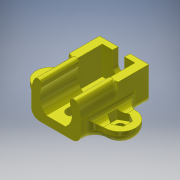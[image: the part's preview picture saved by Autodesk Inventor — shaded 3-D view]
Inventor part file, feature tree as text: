
AUTODESK INVENTOR PART (.ipt)
format: ipt  version: 2019.4 (Build 234330000, 330)  size: 492,544 bytes
history: native  units: mm
features: extrude x18, other x12, sketch x9, fillet x8, projected_geometry x3, chamfer x1, mirror x1
ambient origin geometry x8: Origin, YZ Plane, XZ Plane, XY Plane, X Axis, Y Axis, Z Axis, Center Point
bodies: Solid1 (feature_tree)
feature tree (52):
  extrude  "Body Clip Bulk"  Depth=7.0mm
  fillet  "Clip Bottom Fillet"  Radius=5.0mm
  other  "BC Midplane"
  extrude  "BC Top Cut"  Depth=3.0mm
  fillet  "BC Top Edge Fillets"  Radius=3.0mm
  extrude  "BC Removal Slot"  Depth=13.8mm
  extrude  "FS Floor Bulk"  Depth=2.0mm
  fillet  "FS Bottom Fillet"  Radius=10.4mm
  extrude  "FS Walls"  Depth=15.0mm
  extrude  "FS Front Shaft Seat"  Depth=1.4mm
  extrude  "FS Pillars"  Depth=2.6mm
  extrude  "BC 45deg cut"  TaperAngle=0.0deg  [1 undecoded]
  other  "Encoder Section Plane"
  extrude  "ES Floor"  Depth=10.0mm
  fillet  "ES Bottom Fillet"  Radius=2.0mm
  extrude  "ES Walls"  Depth=3.0mm
  extrude  "ES Slot"  Depth=10.0mm
  extrude  "ES Rear Cutaway"  Depth=10.0mm
  fillet  "ES Merge Fillet"  Radius=10.4mm
  fillet  "ES Cutaway Fille"  [1 undecoded]
  extrude  "ES Pins Undercut"  Depth=9.0mm
  chamfer  "ES Pins Undercut CHamfer"  Distance=7.8mm
  other  "Midplane"
  extrude  "Wing Bulk"  Depth=4.4mm
  extrude  "Wing Underside Merge"  Depth=10.0mm
  fillet  "Wing UNderside Fillet"  Radius=4.4mm
  extrude  "Wing Nut Cut"  Depth=2.0mm
  mirror  "Wing Mirror"
  fillet  "Wings Top Fillet"  [1 undecoded]
  extrude  "Slot Enlarging"  Depth=10.0mm
  extrude  "Extrusion18"  Depth=10.0mm
  other  "Body  Clip Bulk OL"
  other  "BC Top Cut OL"
  other  "FS Floor Bulk OL"
  other  "FS Walls OL"
  other  "FS Shaft Slot Seat OL"
  other  "FS Pillars OL"
  sketch  "Sketch9"  dims[d1=7.0mm d3=12.0mm d4=5.0mm]
  sketch  "Sketch10"  dims[d5=10.0mm d6=3.0mm d8=3.0mm]
  other  "ES walls OL"
  other  "ES Slot ol"
  sketch  "Sketch13"  dims[d9=18.0mm d10=13.8mm]
  other  "BC Removal Slot OL"
  sketch  "Sketch16"  dims[d11=0.0mm d12=2.0mm d13=10.4mm]
  projected_geometry  "Projected Loop1"
  sketch  "Sketch17"  dims[d14=13.8mm d15=15.0mm]
  sketch  "Sketch18"  dims[d16=0.0mm d18=1.4mm]
  projected_geometry  "Projected Loop2"
  sketch  "Sketch19"  dims[d19=18.0mm d20=2.6mm]
  sketch  "Sketch20"  dims[d21=11.2mm d22=0.0mm]
  projected_geometry  "Projected Loop3"
  sketch  "Sketch21"  dims[d23=3.0mm d24=6.8mm d25=2.0mm d26=3.0mm d27=9.2mm d28=11.2mm d30=10.4mm d31=0.0mm d32=9.0mm d33=7.8mm d34=4.4mm d35=5.2mm d36=4.4mm d37=2.0mm d38=0.0mm d39=0.6mm d40=1.9mm d41=6.0mm d42=0.0mm d43=0.6mm d44=3.9mm d46=6.0mm d47=2.3mm d48=3.0mm d49=0.0mm d50=135.0deg d51=3.0mm d52=0.0mm d53=13.8mm d54=2.0mm d55=18.0mm d56=9.1mm d57=0.0mm d58=3.0mm d59=2.3mm d60=2.0mm d61=9.1mm d62=18.0mm d63=11.0mm d64=0.0mm d65=13.8mm d66=3.4mm d67=3.5mm d68=10.0mm d69=0.0mm d70=7.0mm d71=8.9mm d72=10.0mm d73=0.0mm d74=0.95mm d75=3.0mm d79=6.0mm d80=4.0mm d81=10.0mm d82=0.0mm d83=1.8mm d84=0.0mm d85=2.0mm d86=2.0mm d87=45.0deg d88=3.2mm d89=25.2mm d90=11.2mm d91=5.6mm d92=4.4mm d93=0.0mm d94=7.0mm d95=0.0mm d96=-14.0mm d97=3.0mm d98=5.8mm d99=2.4mm d100=0.0mm d102=3.0mm d103=1.1mm d104=0.0mm d105=10.0mm d106=0.0mm]
note: 3 required parameter values undecoded (feature->parameter linkage not recoverable at this tier; creation-order binding heuristic only, values carry confidence <= 0.55)
